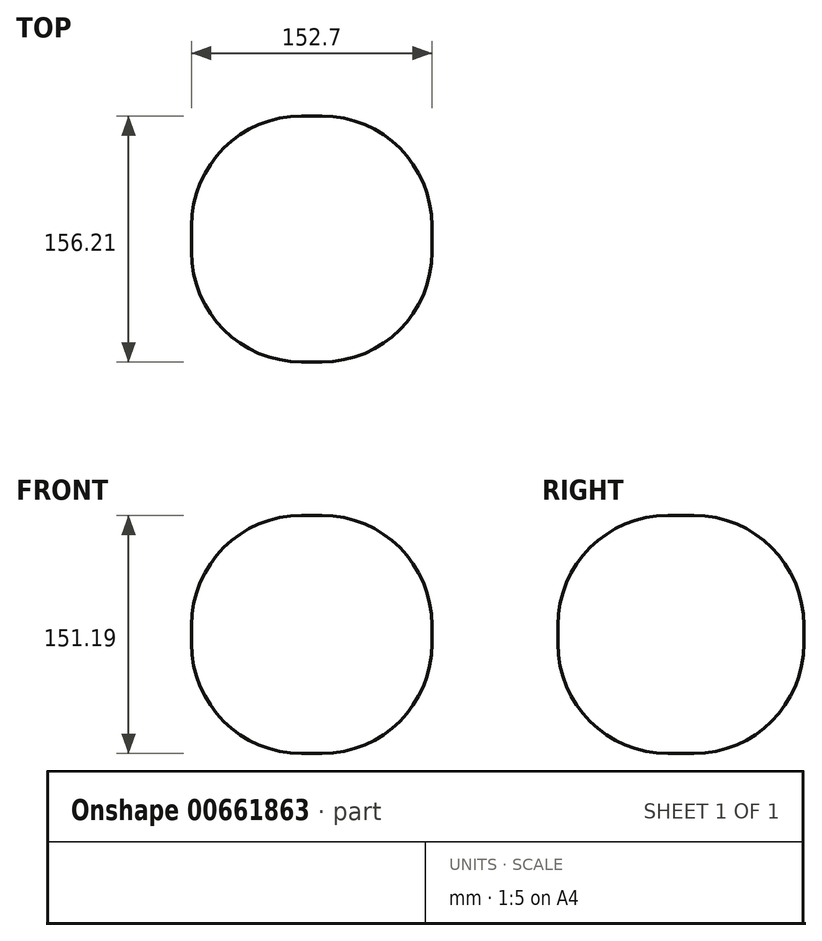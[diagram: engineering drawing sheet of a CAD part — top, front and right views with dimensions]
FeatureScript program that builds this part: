
annotation { "Feature Type Name" : "Feature", "Feature Type Description" : "" }
export const myFeature = defineFeature(function(context is Context, id is Id, definition is map)
    precondition{}
    {
        {
            var Q0;
            Q0=qCreatedBy(makeId("Front.planeOp"),FACE);
            var sketch = newSketch(context, id + "F0", { "sketchPlane" : qUnion([Q0])});
            skLineSegment(sketch, "E0.bottom", {"start": v(-76.4, -75.97) * mm, "end": v(76.31, -75.97) * mm});
            skLineSegment(sketch, "E0.top", {"start": v(-76.4, 75.22) * mm, "end": v(76.31, 75.22) * mm});
            skLineSegment(sketch, "E0.left", {"start": v(-76.4, -75.97) * mm, "end": v(-76.4, 75.22) * mm});
            skLineSegment(sketch, "E0.right", {"start": v(76.31, -75.97) * mm, "end": v(76.31, 75.22) * mm});
            skSolve(sketch);
        }
        {
            var Q0;
            Q0=makeQuery(id+"F0.imprint","IMPRINT",FACE,{"disambiguationData":[TD([[makeQuery(id+"F0.imprint","IMPRINT",EDGE,{"derivedFrom":sQuery(id+"F0.wireOp",EDGE,"E0.bottom")}),1.0]])]});
            extrude(context, id + "F1", {"entities" : qUnion([Q0]), "depth" : 156.21 * mm, "offsetDistance" : 25.4 * mm});
        }
        {
            var Q0;
            Q0=makeQuery(id+"F1.opExtrude","CAP_EDGE",EDGE,{"disambiguationData":[OSD([sQuery(id+"F0.wireOp",EDGE,"E0.top")])],"isStart":false});
            var Q1;
            Q1=makeQuery(id+"F1.opExtrude","CAP_EDGE",EDGE,{"disambiguationData":[OSD([sQuery(id+"F0.wireOp",EDGE,"E0.right")])],"isStart":false});
            var Q2;
            Q2=makeQuery(id+"F1.opExtrude","CAP_EDGE",EDGE,{"disambiguationData":[OSD([sQuery(id+"F0.wireOp",EDGE,"E0.bottom")])],"isStart":false});
            var Q3;
            Q3=makeQuery(id+"F1.opExtrude","CAP_EDGE",EDGE,{"disambiguationData":[OSD([sQuery(id+"F0.wireOp",EDGE,"E0.left")])],"isStart":false});
            var Q4;
            Q4=makeQuery(id+"F1.opExtrude","SWEPT_EDGE",EDGE,{"disambiguationData":[OSD([sQuery(id+"F0.wireOp",EDGE,"E0.top"),sQuery(id+"F0.wireOp",EDGE,"E0.right")])]});
            var Q5;
            Q5=makeQuery(id+"F1.opExtrude","SWEPT_EDGE",EDGE,{"disambiguationData":[OSD([sQuery(id+"F0.wireOp",EDGE,"E0.top"),sQuery(id+"F0.wireOp",EDGE,"E0.left")])]});
            var Q6;
            Q6=makeQuery(id+"F1.opExtrude","CAP_EDGE",EDGE,{"disambiguationData":[OSD([sQuery(id+"F0.wireOp",EDGE,"E0.top")])],"isStart":true});
            var Q7;
            Q7=makeQuery(id+"F1.opExtrude","SWEPT_EDGE",EDGE,{"disambiguationData":[OSD([sQuery(id+"F0.wireOp",EDGE,"E0.bottom"),sQuery(id+"F0.wireOp",EDGE,"E0.right")])]});
            var Q8;
            Q8=makeQuery(id+"F1.opExtrude","SWEPT_FACE",FACE,{"disambiguationData":[OSD([sQuery(id+"F0.wireOp",EDGE,"E0.right")])]});
            var Q9;
            Q9=makeQuery(id+"F1.opExtrude","CAP_EDGE",EDGE,{"disambiguationData":[OSD([sQuery(id+"F0.wireOp",EDGE,"E0.left")])],"isStart":true});
            var Q10;
            Q10=makeQuery(id+"F1.opExtrude","CAP_EDGE",EDGE,{"disambiguationData":[OSD([sQuery(id+"F0.wireOp",EDGE,"E0.bottom")])],"isStart":true});
            var Q11;
            Q11=makeQuery(id+"F1.opExtrude","SWEPT_EDGE",EDGE,{"disambiguationData":[OSD([sQuery(id+"F0.wireOp",EDGE,"E0.bottom"),sQuery(id+"F0.wireOp",EDGE,"E0.left")])]});
            fillet(context, id + "F2", {"entities" : qUnion([Q0, Q1, Q2, Q3, Q4, Q5, Q6, Q7, Q8, Q9, Q10, Q11]), "radius" : 69.85 * mm, "tangentPropagation" : true, "allowEdgeOverflow" : false});
        }
    });
